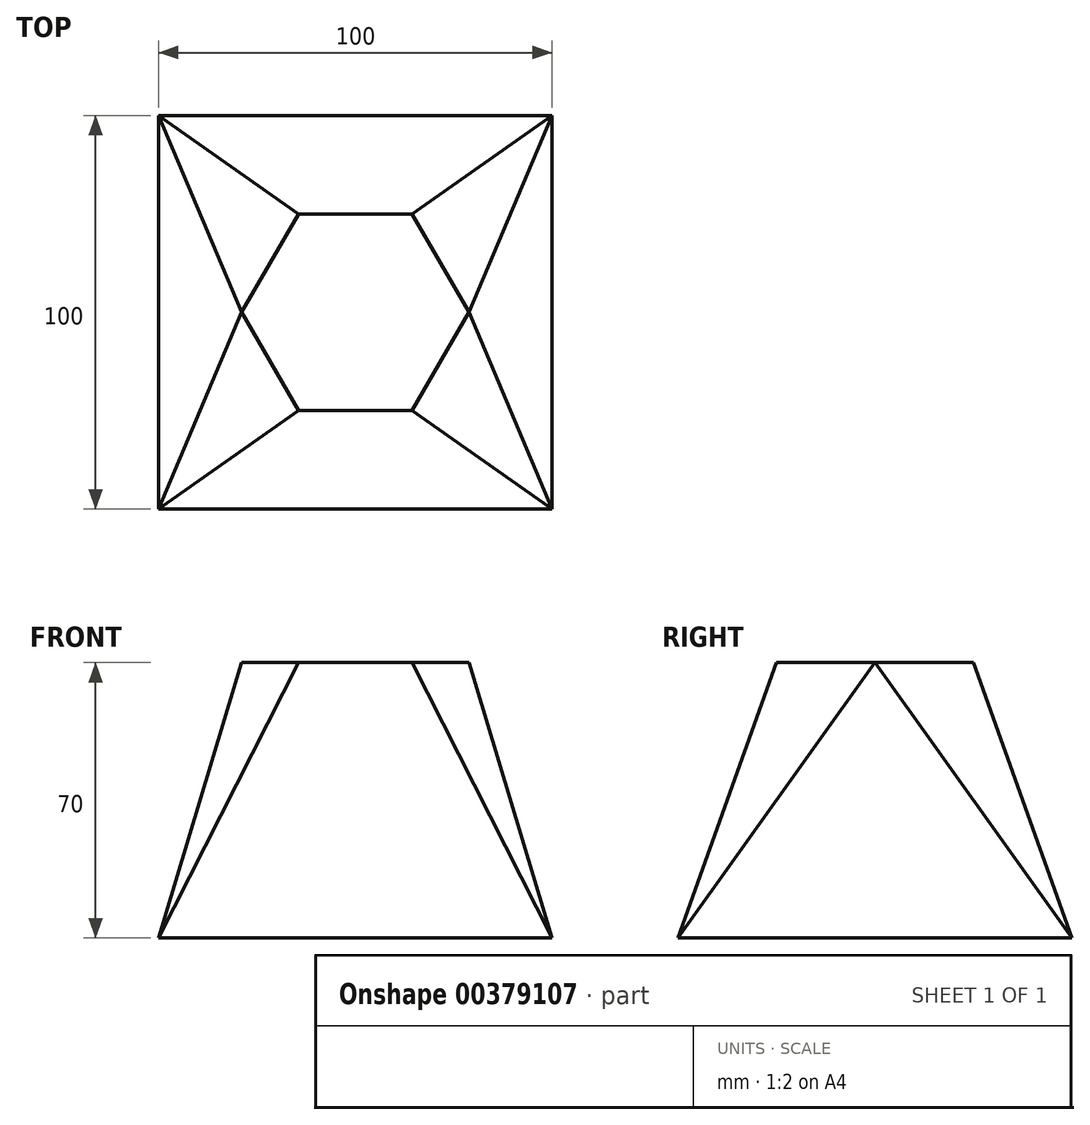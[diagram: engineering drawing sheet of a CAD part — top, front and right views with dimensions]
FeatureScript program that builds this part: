
annotation { "Feature Type Name" : "Feature", "Feature Type Description" : "" }
export const myFeature = defineFeature(function(context is Context, id is Id, definition is map)
    precondition{}
    {
        {
            var Q0;
            Q0=qCreatedBy(makeId("Top.planeOp"),FACE);
            var sketch = newSketch(context, id + "F0", { "sketchPlane" : qUnion([Q0])});
            skLineSegment(sketch, "E0.bottom", {"start": v(50, 50) * mm, "end": v(-50, 50) * mm});
            skLineSegment(sketch, "E0.top", {"start": v(50, -50) * mm, "end": v(-50, -50) * mm});
            skLineSegment(sketch, "E0.left", {"start": v(50, 50) * mm, "end": v(50, -50) * mm});
            skLineSegment(sketch, "E0.right", {"start": v(-50, 50) * mm, "end": v(-50, -50) * mm});
            skPoint(sketch, "E0.middle", {"position": v(0, 0) * mm});
            skSolve(sketch);
        }
        {
            var Q0;
            Q0=qCreatedBy(makeId("Top.planeOp"),FACE);
            cPlane(context, id + "F1", {"entities" : qUnion([Q0]), "cplaneType" : CPlaneType.OFFSET, "offset" : 70 * mm, "width" : 150 * mm, "height" : 150 * mm});
        }
        {
            var Q0;
            Q0=qCreatedBy(id+"F1.planeOp",FACE);
            var sketch = newSketch(context, id + "F2", { "sketchPlane" : qUnion([Q0])});
            skCircle(sketch, "E1.cCircle", {"center": v(0, 0) * mm, "radius": 28.87 * mm, "construction": true});
            skLineSegment(sketch, "E1.0", {"start": v(28.87, 0) * mm, "end": v(14.43, -25) * mm});
            skLineSegment(sketch, "E1.1", {"start": v(14.43, -25) * mm, "end": v(-14.43, -25) * mm});
            skLineSegment(sketch, "E1.2", {"start": v(-14.43, -25) * mm, "end": v(-28.87, 0) * mm});
            skLineSegment(sketch, "E1.3", {"start": v(-28.87, 0) * mm, "end": v(-14.43, 25) * mm});
            skLineSegment(sketch, "E1.4", {"start": v(-14.43, 25) * mm, "end": v(14.43, 25) * mm});
            skLineSegment(sketch, "E1.5", {"start": v(14.43, 25) * mm, "end": v(28.87, 0) * mm});
            skLineSegment(sketch, "E2", {"start": v(-28.87, 0) * mm, "end": v(-28.87, 25) * mm});
            skLineSegment(sketch, "E3", {"start": v(-28.87, 25) * mm, "end": v(-14.43, 25) * mm});
            skSolve(sketch);
        }
        {
            var Q0;
            Q0=qCreatedBy(id+"F1.planeOp",FACE);
            var sketch = newSketch(context, id + "F3", { "sketchPlane" : qUnion([Q0])});
            skLineSegment(sketch, "E4.bottom", {"start": v(-28.87, 25) * mm, "end": v(28.87, 25) * mm});
            skLineSegment(sketch, "E4.top", {"start": v(-28.87, -25) * mm, "end": v(28.87, -25) * mm});
            skLineSegment(sketch, "E4.left", {"start": v(-28.87, 25) * mm, "end": v(-28.87, -25) * mm});
            skLineSegment(sketch, "E4.right", {"start": v(28.87, 25) * mm, "end": v(28.87, -25) * mm});
            skPoint(sketch, "E4.middle", {"position": v(0, 0) * mm});
            skSolve(sketch);
        }
        {
            var Q0;
            Q0=makeQuery(id+"F0.imprint","IMPRINT",FACE,{"disambiguationData":[TD([[makeQuery(id+"F0.imprint","IMPRINT",EDGE,{"derivedFrom":sQuery(id+"F0.wireOp",EDGE,"E0.bottom")}),1.0]])]});
            var Q1;
            Q1=makeQuery(id+"F3.imprint","IMPRINT",FACE,{"disambiguationData":[TD([[makeQuery(id+"F3.imprint","IMPRINT",EDGE,{"derivedFrom":sQuery(id+"F3.wireOp",EDGE,"E4.bottom")}),-1.0]])]});
            loft(context, id + "F4", {"sheetProfilesArray" : [{ "sheetProfileEntities" : qUnion([Q0]) }, { "sheetProfileEntities" : qUnion([Q1]) }]});
        }
        {
            var Q1;
            Q1=makeQuery(id+"F2.imprint","IMPRINT",FACE,{"disambiguationData":[TD([[makeQuery(id+"F2.imprint","IMPRINT",EDGE,{"derivedFrom":sQuery(id+"F2.wireOp",EDGE,"E1.3")}),1.0]])]});
            var Q2;
            Q2=makeQuery(id+"F4.opLoft","MID_CAP_VERTEX",VERTEX,{"disambiguationData":[OSD([sQuery(id+"F0.wireOp",EDGE,"E0.bottom"),sQuery(id+"F0.wireOp",EDGE,"E0.right")])],"capPos":0.0});
            loft(context, id + "F5", {"sheetProfilesArray" : [{ "sheetProfileEntities" : qUnion([Q1]) }, { "sheetProfileEntities" : qUnion([Q2]) }]});
        }
        {
            var Q0;
            Q0=makeQuery(id+"F5.opLoft","SWEPT_BODY",BODY,{"disambiguationData":[OSD([sQuery(id+"F0.wireOp",EDGE,"E0.bottom"),sQuery(id+"F0.wireOp",EDGE,"E0.right"),makeQuery(id+"F2.imprint","IMPRINT",FACE,{"disambiguationData":[TD([[makeQuery(id+"F2.imprint","IMPRINT",EDGE,{"derivedFrom":sQuery(id+"F2.wireOp",EDGE,"E1.3")}),1.0]])]})])]});
            var Q1;
            Q1=qCreatedBy(makeId("Front.planeOp"),FACE);
            mirror(context, id + "F6", {"entities" : qUnion([Q0]), "mirrorPlane" : qUnion([Q1])});
        }
        {
            var Q0;
            Q0=makeQuery(id+"F5.opLoft","SWEPT_BODY",BODY,{"disambiguationData":[OSD([sQuery(id+"F0.wireOp",EDGE,"E0.bottom"),sQuery(id+"F0.wireOp",EDGE,"E0.right"),makeQuery(id+"F2.imprint","IMPRINT",FACE,{"disambiguationData":[TD([[makeQuery(id+"F2.imprint","IMPRINT",EDGE,{"derivedFrom":sQuery(id+"F2.wireOp",EDGE,"E1.3")}),1.0]])]})])]});
            var Q1;
            Q1=makeQuery(id+"F6.opPattern","COPY",BODY,{"derivedFrom":makeQuery(id+"F5.opLoft","SWEPT_BODY",BODY,{"disambiguationData":[OSD([sQuery(id+"F0.wireOp",EDGE,"E0.bottom"),sQuery(id+"F0.wireOp",EDGE,"E0.right"),makeQuery(id+"F2.imprint","IMPRINT",FACE,{"disambiguationData":[TD([[makeQuery(id+"F2.imprint","IMPRINT",EDGE,{"derivedFrom":sQuery(id+"F2.wireOp",EDGE,"E1.3")}),1.0]])]})])]}),"instanceName":"1"});
            var Q2;
            Q2=qCreatedBy(makeId("Right.planeOp"),FACE);
            mirror(context, id + "F7", {"entities" : qUnion([Q0, Q1]), "mirrorPlane" : qUnion([Q2])});
        }
        {
            var Q0;
            Q0=makeQuery(id+"F5.opLoft","SWEPT_BODY",BODY,{"disambiguationData":[OSD([sQuery(id+"F0.wireOp",EDGE,"E0.bottom"),sQuery(id+"F0.wireOp",EDGE,"E0.right"),makeQuery(id+"F2.imprint","IMPRINT",FACE,{"disambiguationData":[TD([[makeQuery(id+"F2.imprint","IMPRINT",EDGE,{"derivedFrom":sQuery(id+"F2.wireOp",EDGE,"E1.3")}),1.0]])]})])]});
            var Q1;
            Q1=makeQuery(id+"F6.opPattern","COPY",BODY,{"derivedFrom":makeQuery(id+"F5.opLoft","SWEPT_BODY",BODY,{"disambiguationData":[OSD([sQuery(id+"F0.wireOp",EDGE,"E0.bottom"),sQuery(id+"F0.wireOp",EDGE,"E0.right"),makeQuery(id+"F2.imprint","IMPRINT",FACE,{"disambiguationData":[TD([[makeQuery(id+"F2.imprint","IMPRINT",EDGE,{"derivedFrom":sQuery(id+"F2.wireOp",EDGE,"E1.3")}),1.0]])]})])]}),"instanceName":"1"});
            var Q2;
            Q2=makeQuery(id+"F7.opPattern","COPY",BODY,{"derivedFrom":makeQuery(id+"F5.opLoft","SWEPT_BODY",BODY,{"disambiguationData":[OSD([sQuery(id+"F0.wireOp",EDGE,"E0.bottom"),sQuery(id+"F0.wireOp",EDGE,"E0.right"),makeQuery(id+"F2.imprint","IMPRINT",FACE,{"disambiguationData":[TD([[makeQuery(id+"F2.imprint","IMPRINT",EDGE,{"derivedFrom":sQuery(id+"F2.wireOp",EDGE,"E1.3")}),1.0]])]})])]}),"instanceName":"1"});
            var Q3;
            Q3=makeQuery(id+"F7.opPattern","COPY",BODY,{"derivedFrom":makeQuery(id+"F6.opPattern","COPY",BODY,{"derivedFrom":makeQuery(id+"F5.opLoft","SWEPT_BODY",BODY,{"disambiguationData":[OSD([sQuery(id+"F0.wireOp",EDGE,"E0.bottom"),sQuery(id+"F0.wireOp",EDGE,"E0.right"),makeQuery(id+"F2.imprint","IMPRINT",FACE,{"disambiguationData":[TD([[makeQuery(id+"F2.imprint","IMPRINT",EDGE,{"derivedFrom":sQuery(id+"F2.wireOp",EDGE,"E1.3")}),1.0]])]})])]}),"instanceName":"1"}),"instanceName":"1"});
            var Q4;
            Q4=makeQuery(id+"F4.opLoft","SWEPT_BODY",BODY,{"disambiguationData":[OSD([makeQuery(id+"F0.imprint","IMPRINT",FACE,{"disambiguationData":[TD([[makeQuery(id+"F0.imprint","IMPRINT",EDGE,{"derivedFrom":sQuery(id+"F0.wireOp",EDGE,"E0.bottom")}),1.0]])]}),makeQuery(id+"F3.imprint","IMPRINT",FACE,{"disambiguationData":[TD([[makeQuery(id+"F3.imprint","IMPRINT",EDGE,{"derivedFrom":sQuery(id+"F3.wireOp",EDGE,"E4.bottom")}),-1.0]])]})])]});
            booleanBodies(context, id + "F8", {"operationType" : BooleanOperationType.SUBTRACTION, "tools" : qUnion([Q0, Q1, Q2, Q3]), "targets" : qUnion([Q4])});
        }
    });
